# Revit family: Specialty Equipment_Coat Hook_Metlam_ML415831216eb1-110b-4046-add7-53dfd6caf8df
name_source: partatom
category: Specialty Equipment
revit_build: Autodesk Revit 2014 (Build: 20130308_1515(x64)
units: mm (PartAtom-declared; Revit-internal decimal feet)

## types (1)
- 20w x 74h x 44d
    Assembly Code = C1030200
    Description = Coat Hook
    Manufacturer = Metlam
    Manufacturer_Overall Depth = 44 mm  [stored 0.144357 ft]
    Manufacturer_Overall Height = 74 mm  [stored 0.242782 ft]
    Manufacturer_Overall Width = 20 mm  [stored 0.0656168 ft]
    Manufacturer_Spec Code = ML4158
    Manufacturer_URL__Product Specific = http://www.metlam.com.au
    Material = z_Metlam_Metal_Stainless Steel Satin
    Model = ML4158
    ModifiedIssue_ANZRS = 20150127 $
    Type Comments = ML4158
    URL = www.metlam.com.au

note: [stored X ft] marks values corroborated as IEEE doubles in the binary element streams (Revit-internal decimal feet)

## geometry (parser evidence)
native form markers: Sweep x3
no freeform markers — native parametric forms only
